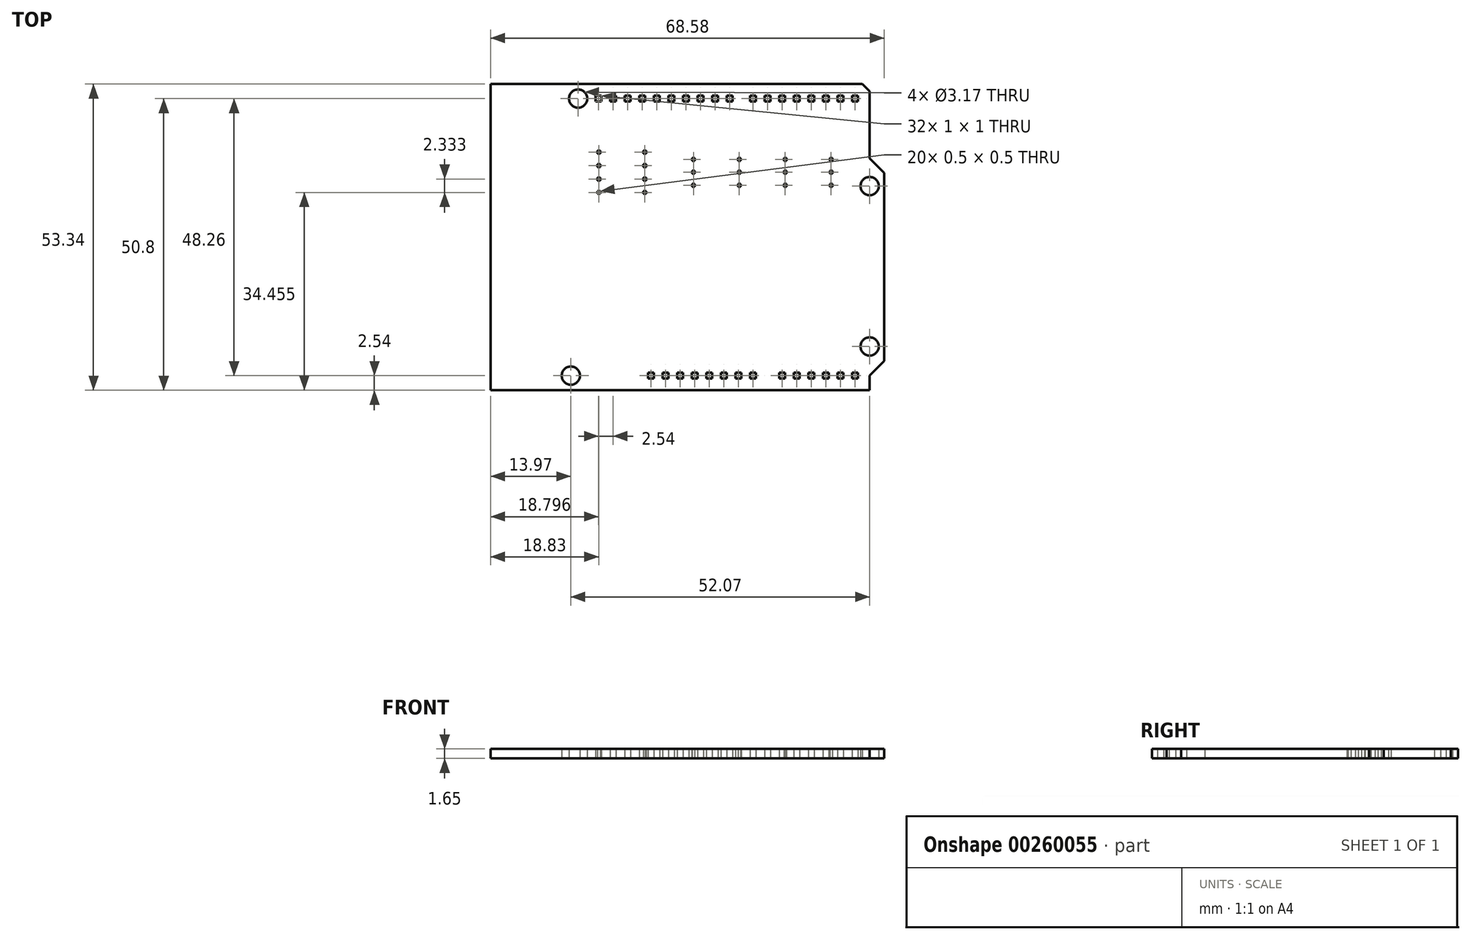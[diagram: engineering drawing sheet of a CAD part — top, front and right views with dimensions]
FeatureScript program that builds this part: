
annotation { "Feature Type Name" : "Feature", "Feature Type Description" : "" }
export const myFeature = defineFeature(function(context is Context, id is Id, definition is map)
    precondition{}
    {
        {
            var Q0;
            Q0=qCreatedBy(makeId("Top.planeOp"),FACE);
            var sketch = newSketch(context, id + "F0", { "sketchPlane" : qUnion([Q0])});
            skLineSegment(sketch, "E0", {"start": v(0, 0) * mm, "end": v(0, 53.34) * mm});
            skLineSegment(sketch, "E1", {"start": v(0, 53.34) * mm, "end": v(64.77, 53.34) * mm});
            skLineSegment(sketch, "E2", {"start": v(66.04, 52.07) * mm, "end": v(66.04, 40.39) * mm});
            skLineSegment(sketch, "E3", {"start": v(68.58, 37.85) * mm, "end": v(68.58, 5.08) * mm});
            skLineSegment(sketch, "E4", {"start": v(66.04, 0) * mm, "end": v(0, 0) * mm});
            skLineSegment(sketch, "E5", {"start": v(66.04, 40.39) * mm, "end": v(68.58, 37.85) * mm});
            skLineSegment(sketch, "E6", {"start": v(68.58, 5.08) * mm, "end": v(66.04, 2.54) * mm});
            skLineSegment(sketch, "E7", {"start": v(66.04, 2.54) * mm, "end": v(66.04, 0) * mm});
            skPoint(sketch, "E8.orphan", {"position": v(68.58, 0) * mm});
            skLineSegment(sketch, "E9", {"start": v(64.77, 53.34) * mm, "end": v(66.04, 52.07) * mm});
            skCircle(sketch, "E10", {"center": v(15.24, 50.8) * mm, "radius": 1.59 * mm});
            skCircle(sketch, "E11", {"center": v(66.04, 35.56) * mm, "radius": 1.59 * mm});
            skCircle(sketch, "E12", {"center": v(13.97, 2.54) * mm, "radius": 1.59 * mm});
            skCircle(sketch, "E13", {"center": v(66.04, 7.62) * mm, "radius": 1.59 * mm});
            skLineSegment(sketch, "E14.bottom", {"start": v(63, 3.04) * mm, "end": v(64, 3.04) * mm});
            skLineSegment(sketch, "E14.top", {"start": v(63, 2.04) * mm, "end": v(64, 2.04) * mm});
            skLineSegment(sketch, "E14.left", {"start": v(63, 3.04) * mm, "end": v(63, 2.04) * mm});
            skLineSegment(sketch, "E14.right", {"start": v(64, 3.04) * mm, "end": v(64, 2.04) * mm});
            skLineSegment(sketch, "E15", {"start": v(66.04, 2.54) * mm, "end": v(0, 2.54) * mm, "construction": true});
            skLineSegment(sketch, "E16.1.0.0", {"start": v(60.46, 3.04) * mm, "end": v(61.46, 3.04) * mm});
            skLineSegment(sketch, "E16.1.0.1", {"start": v(60.46, 3.04) * mm, "end": v(60.46, 2.04) * mm});
            skLineSegment(sketch, "E16.1.0.2", {"start": v(60.46, 2.04) * mm, "end": v(61.46, 2.04) * mm});
            skLineSegment(sketch, "E16.1.0.3", {"start": v(61.46, 3.04) * mm, "end": v(61.46, 2.04) * mm});
            skLineSegment(sketch, "E16.2.0.0", {"start": v(57.92, 3.04) * mm, "end": v(58.92, 3.04) * mm});
            skLineSegment(sketch, "E16.2.0.1", {"start": v(57.92, 3.04) * mm, "end": v(57.92, 2.04) * mm});
            skLineSegment(sketch, "E16.2.0.2", {"start": v(57.92, 2.04) * mm, "end": v(58.92, 2.04) * mm});
            skLineSegment(sketch, "E16.2.0.3", {"start": v(58.92, 3.04) * mm, "end": v(58.92, 2.04) * mm});
            skLineSegment(sketch, "E16.3.0.0", {"start": v(55.38, 3.04) * mm, "end": v(56.38, 3.04) * mm});
            skLineSegment(sketch, "E16.3.0.1", {"start": v(55.38, 3.04) * mm, "end": v(55.38, 2.04) * mm});
            skLineSegment(sketch, "E16.3.0.2", {"start": v(55.38, 2.04) * mm, "end": v(56.38, 2.04) * mm});
            skLineSegment(sketch, "E16.3.0.3", {"start": v(56.38, 3.04) * mm, "end": v(56.38, 2.04) * mm});
            skLineSegment(sketch, "E16.4.0.0", {"start": v(52.84, 3.04) * mm, "end": v(53.84, 3.04) * mm});
            skLineSegment(sketch, "E16.4.0.1", {"start": v(52.84, 3.04) * mm, "end": v(52.84, 2.04) * mm});
            skLineSegment(sketch, "E16.4.0.2", {"start": v(52.84, 2.04) * mm, "end": v(53.84, 2.04) * mm});
            skLineSegment(sketch, "E16.4.0.3", {"start": v(53.84, 3.04) * mm, "end": v(53.84, 2.04) * mm});
            skLineSegment(sketch, "E16.5.0.0", {"start": v(50.3, 3.04) * mm, "end": v(51.3, 3.04) * mm});
            skLineSegment(sketch, "E16.5.0.1", {"start": v(50.3, 3.04) * mm, "end": v(50.3, 2.04) * mm});
            skLineSegment(sketch, "E16.5.0.2", {"start": v(50.3, 2.04) * mm, "end": v(51.3, 2.04) * mm});
            skLineSegment(sketch, "E16.5.0.3", {"start": v(51.3, 3.04) * mm, "end": v(51.3, 2.04) * mm});
            skLineSegment(sketch, "E16.direction1", {"start": v(63, 3.04) * mm, "end": v(60.46, 3.04) * mm, "construction": true});
            skLineSegment(sketch, "E17.bottom", {"start": v(45.22, 3.04) * mm, "end": v(46.22, 3.04) * mm});
            skLineSegment(sketch, "E17.top", {"start": v(45.22, 2.04) * mm, "end": v(46.22, 2.04) * mm});
            skLineSegment(sketch, "E17.left", {"start": v(45.22, 3.04) * mm, "end": v(45.22, 2.04) * mm});
            skLineSegment(sketch, "E17.right", {"start": v(46.22, 3.04) * mm, "end": v(46.22, 2.04) * mm});
            skLineSegment(sketch, "E18.1.0.0", {"start": v(42.68, 3.04) * mm, "end": v(43.68, 3.04) * mm});
            skLineSegment(sketch, "E18.1.0.1", {"start": v(42.68, 3.04) * mm, "end": v(42.68, 2.04) * mm});
            skLineSegment(sketch, "E18.1.0.2", {"start": v(42.68, 2.04) * mm, "end": v(43.68, 2.04) * mm});
            skLineSegment(sketch, "E18.1.0.3", {"start": v(43.68, 3.04) * mm, "end": v(43.68, 2.04) * mm});
            skLineSegment(sketch, "E18.2.0.0", {"start": v(40.14, 3.04) * mm, "end": v(41.14, 3.04) * mm});
            skLineSegment(sketch, "E18.2.0.1", {"start": v(40.14, 3.04) * mm, "end": v(40.14, 2.04) * mm});
            skLineSegment(sketch, "E18.2.0.2", {"start": v(40.14, 2.04) * mm, "end": v(41.14, 2.04) * mm});
            skLineSegment(sketch, "E18.2.0.3", {"start": v(41.14, 3.04) * mm, "end": v(41.14, 2.04) * mm});
            skLineSegment(sketch, "E18.3.0.0", {"start": v(37.6, 3.04) * mm, "end": v(38.6, 3.04) * mm});
            skLineSegment(sketch, "E18.3.0.1", {"start": v(37.6, 3.04) * mm, "end": v(37.6, 2.04) * mm});
            skLineSegment(sketch, "E18.3.0.2", {"start": v(37.6, 2.04) * mm, "end": v(38.6, 2.04) * mm});
            skLineSegment(sketch, "E18.3.0.3", {"start": v(38.6, 3.04) * mm, "end": v(38.6, 2.04) * mm});
            skLineSegment(sketch, "E18.4.0.0", {"start": v(35.06, 3.04) * mm, "end": v(36.06, 3.04) * mm});
            skLineSegment(sketch, "E18.4.0.1", {"start": v(35.06, 3.04) * mm, "end": v(35.06, 2.04) * mm});
            skLineSegment(sketch, "E18.4.0.2", {"start": v(35.06, 2.04) * mm, "end": v(36.06, 2.04) * mm});
            skLineSegment(sketch, "E18.4.0.3", {"start": v(36.06, 3.04) * mm, "end": v(36.06, 2.04) * mm});
            skLineSegment(sketch, "E18.5.0.0", {"start": v(32.52, 3.04) * mm, "end": v(33.52, 3.04) * mm});
            skLineSegment(sketch, "E18.5.0.1", {"start": v(32.52, 3.04) * mm, "end": v(32.52, 2.04) * mm});
            skLineSegment(sketch, "E18.5.0.2", {"start": v(32.52, 2.04) * mm, "end": v(33.52, 2.04) * mm});
            skLineSegment(sketch, "E18.5.0.3", {"start": v(33.52, 3.04) * mm, "end": v(33.52, 2.04) * mm});
            skLineSegment(sketch, "E18.6.0.0", {"start": v(29.98, 3.04) * mm, "end": v(30.98, 3.04) * mm});
            skLineSegment(sketch, "E18.6.0.1", {"start": v(29.98, 3.04) * mm, "end": v(29.98, 2.04) * mm});
            skLineSegment(sketch, "E18.6.0.2", {"start": v(29.98, 2.04) * mm, "end": v(30.98, 2.04) * mm});
            skLineSegment(sketch, "E18.6.0.3", {"start": v(30.98, 3.04) * mm, "end": v(30.98, 2.04) * mm});
            skLineSegment(sketch, "E18.7.0.0", {"start": v(27.44, 3.04) * mm, "end": v(28.44, 3.04) * mm});
            skLineSegment(sketch, "E18.7.0.1", {"start": v(27.44, 3.04) * mm, "end": v(27.44, 2.04) * mm});
            skLineSegment(sketch, "E18.7.0.2", {"start": v(27.44, 2.04) * mm, "end": v(28.44, 2.04) * mm});
            skLineSegment(sketch, "E18.7.0.3", {"start": v(28.44, 3.04) * mm, "end": v(28.44, 2.04) * mm});
            skLineSegment(sketch, "E18.direction1", {"start": v(45.22, 3.04) * mm, "end": v(42.68, 3.04) * mm, "construction": true});
            skLineSegment(sketch, "E19", {"start": v(66.04, 50.8) * mm, "end": v(0, 50.8) * mm, "construction": true});
            skLineSegment(sketch, "E20.bottom", {"start": v(63, 51.3) * mm, "end": v(64, 51.3) * mm});
            skLineSegment(sketch, "E20.top", {"start": v(63, 50.3) * mm, "end": v(64, 50.3) * mm});
            skLineSegment(sketch, "E20.left", {"start": v(63, 51.3) * mm, "end": v(63, 50.3) * mm});
            skLineSegment(sketch, "E20.right", {"start": v(64, 51.3) * mm, "end": v(64, 50.3) * mm});
            skLineSegment(sketch, "E21.1.0.0", {"start": v(60.46, 51.3) * mm, "end": v(60.46, 50.3) * mm});
            skLineSegment(sketch, "E21.1.0.1", {"start": v(60.46, 51.3) * mm, "end": v(61.46, 51.3) * mm});
            skLineSegment(sketch, "E21.1.0.2", {"start": v(61.46, 51.3) * mm, "end": v(61.46, 50.3) * mm});
            skLineSegment(sketch, "E21.1.0.3", {"start": v(60.46, 50.3) * mm, "end": v(61.46, 50.3) * mm});
            skLineSegment(sketch, "E21.2.0.0", {"start": v(57.92, 51.3) * mm, "end": v(57.92, 50.3) * mm});
            skLineSegment(sketch, "E21.2.0.1", {"start": v(57.92, 51.3) * mm, "end": v(58.92, 51.3) * mm});
            skLineSegment(sketch, "E21.2.0.2", {"start": v(58.92, 51.3) * mm, "end": v(58.92, 50.3) * mm});
            skLineSegment(sketch, "E21.2.0.3", {"start": v(57.92, 50.3) * mm, "end": v(58.92, 50.3) * mm});
            skLineSegment(sketch, "E21.3.0.0", {"start": v(55.38, 51.3) * mm, "end": v(55.38, 50.3) * mm});
            skLineSegment(sketch, "E21.3.0.1", {"start": v(55.38, 51.3) * mm, "end": v(56.38, 51.3) * mm});
            skLineSegment(sketch, "E21.3.0.2", {"start": v(56.38, 51.3) * mm, "end": v(56.38, 50.3) * mm});
            skLineSegment(sketch, "E21.3.0.3", {"start": v(55.38, 50.3) * mm, "end": v(56.38, 50.3) * mm});
            skLineSegment(sketch, "E21.4.0.0", {"start": v(52.84, 51.3) * mm, "end": v(52.84, 50.3) * mm});
            skLineSegment(sketch, "E21.4.0.1", {"start": v(52.84, 51.3) * mm, "end": v(53.84, 51.3) * mm});
            skLineSegment(sketch, "E21.4.0.2", {"start": v(53.84, 51.3) * mm, "end": v(53.84, 50.3) * mm});
            skLineSegment(sketch, "E21.4.0.3", {"start": v(52.84, 50.3) * mm, "end": v(53.84, 50.3) * mm});
            skLineSegment(sketch, "E21.5.0.0", {"start": v(50.3, 51.3) * mm, "end": v(50.3, 50.3) * mm});
            skLineSegment(sketch, "E21.5.0.1", {"start": v(50.3, 51.3) * mm, "end": v(51.3, 51.3) * mm});
            skLineSegment(sketch, "E21.5.0.2", {"start": v(51.3, 51.3) * mm, "end": v(51.3, 50.3) * mm});
            skLineSegment(sketch, "E21.5.0.3", {"start": v(50.3, 50.3) * mm, "end": v(51.3, 50.3) * mm});
            skLineSegment(sketch, "E21.6.0.0", {"start": v(47.76, 51.3) * mm, "end": v(47.76, 50.3) * mm});
            skLineSegment(sketch, "E21.6.0.1", {"start": v(47.76, 51.3) * mm, "end": v(48.76, 51.3) * mm});
            skLineSegment(sketch, "E21.6.0.2", {"start": v(48.76, 51.3) * mm, "end": v(48.76, 50.3) * mm});
            skLineSegment(sketch, "E21.6.0.3", {"start": v(47.76, 50.3) * mm, "end": v(48.76, 50.3) * mm});
            skLineSegment(sketch, "E21.7.0.0", {"start": v(45.22, 51.3) * mm, "end": v(45.22, 50.3) * mm});
            skLineSegment(sketch, "E21.7.0.1", {"start": v(45.22, 51.3) * mm, "end": v(46.22, 51.3) * mm});
            skLineSegment(sketch, "E21.7.0.2", {"start": v(46.22, 51.3) * mm, "end": v(46.22, 50.3) * mm});
            skLineSegment(sketch, "E21.7.0.3", {"start": v(45.22, 50.3) * mm, "end": v(46.22, 50.3) * mm});
            skLineSegment(sketch, "E21.direction1", {"start": v(63, 50.3) * mm, "end": v(60.46, 50.3) * mm, "construction": true});
            skLineSegment(sketch, "E22.bottom", {"start": v(41.16, 51.3) * mm, "end": v(42.16, 51.3) * mm});
            skLineSegment(sketch, "E22.top", {"start": v(41.16, 50.3) * mm, "end": v(42.16, 50.3) * mm});
            skLineSegment(sketch, "E22.left", {"start": v(41.16, 51.3) * mm, "end": v(41.16, 50.3) * mm});
            skLineSegment(sketch, "E22.right", {"start": v(42.16, 51.3) * mm, "end": v(42.16, 50.3) * mm});
            skLineSegment(sketch, "E23.1.0.0", {"start": v(38.62, 51.3) * mm, "end": v(39.62, 51.3) * mm});
            skLineSegment(sketch, "E23.1.0.1", {"start": v(38.62, 51.3) * mm, "end": v(38.62, 50.3) * mm});
            skLineSegment(sketch, "E23.1.0.2", {"start": v(38.62, 50.3) * mm, "end": v(39.62, 50.3) * mm});
            skLineSegment(sketch, "E23.1.0.3", {"start": v(39.62, 51.3) * mm, "end": v(39.62, 50.3) * mm});
            skLineSegment(sketch, "E23.2.0.0", {"start": v(36.08, 51.3) * mm, "end": v(37.08, 51.3) * mm});
            skLineSegment(sketch, "E23.2.0.1", {"start": v(36.08, 51.3) * mm, "end": v(36.08, 50.3) * mm});
            skLineSegment(sketch, "E23.2.0.2", {"start": v(36.08, 50.3) * mm, "end": v(37.08, 50.3) * mm});
            skLineSegment(sketch, "E23.2.0.3", {"start": v(37.08, 51.3) * mm, "end": v(37.08, 50.3) * mm});
            skLineSegment(sketch, "E23.3.0.0", {"start": v(33.54, 51.3) * mm, "end": v(34.54, 51.3) * mm});
            skLineSegment(sketch, "E23.3.0.1", {"start": v(33.54, 51.3) * mm, "end": v(33.54, 50.3) * mm});
            skLineSegment(sketch, "E23.3.0.2", {"start": v(33.54, 50.3) * mm, "end": v(34.54, 50.3) * mm});
            skLineSegment(sketch, "E23.3.0.3", {"start": v(34.54, 51.3) * mm, "end": v(34.54, 50.3) * mm});
            skLineSegment(sketch, "E23.4.0.0", {"start": v(31, 51.3) * mm, "end": v(32, 51.3) * mm});
            skLineSegment(sketch, "E23.4.0.1", {"start": v(31, 51.3) * mm, "end": v(31, 50.3) * mm});
            skLineSegment(sketch, "E23.4.0.2", {"start": v(31, 50.3) * mm, "end": v(32, 50.3) * mm});
            skLineSegment(sketch, "E23.4.0.3", {"start": v(32, 51.3) * mm, "end": v(32, 50.3) * mm});
            skLineSegment(sketch, "E23.5.0.0", {"start": v(28.46, 51.3) * mm, "end": v(29.46, 51.3) * mm});
            skLineSegment(sketch, "E23.5.0.1", {"start": v(28.46, 51.3) * mm, "end": v(28.46, 50.3) * mm});
            skLineSegment(sketch, "E23.5.0.2", {"start": v(28.46, 50.3) * mm, "end": v(29.46, 50.3) * mm});
            skLineSegment(sketch, "E23.5.0.3", {"start": v(29.46, 51.3) * mm, "end": v(29.46, 50.3) * mm});
            skLineSegment(sketch, "E23.6.0.0", {"start": v(25.92, 51.3) * mm, "end": v(26.92, 51.3) * mm});
            skLineSegment(sketch, "E23.6.0.1", {"start": v(25.92, 51.3) * mm, "end": v(25.92, 50.3) * mm});
            skLineSegment(sketch, "E23.6.0.2", {"start": v(25.92, 50.3) * mm, "end": v(26.92, 50.3) * mm});
            skLineSegment(sketch, "E23.6.0.3", {"start": v(26.92, 51.3) * mm, "end": v(26.92, 50.3) * mm});
            skLineSegment(sketch, "E23.7.0.0", {"start": v(23.38, 51.3) * mm, "end": v(24.38, 51.3) * mm});
            skLineSegment(sketch, "E23.7.0.1", {"start": v(23.38, 51.3) * mm, "end": v(23.38, 50.3) * mm});
            skLineSegment(sketch, "E23.7.0.2", {"start": v(23.38, 50.3) * mm, "end": v(24.38, 50.3) * mm});
            skLineSegment(sketch, "E23.7.0.3", {"start": v(24.38, 51.3) * mm, "end": v(24.38, 50.3) * mm});
            skLineSegment(sketch, "E23.8.0.0", {"start": v(20.84, 51.3) * mm, "end": v(21.84, 51.3) * mm});
            skLineSegment(sketch, "E23.8.0.1", {"start": v(20.84, 51.3) * mm, "end": v(20.84, 50.3) * mm});
            skLineSegment(sketch, "E23.8.0.2", {"start": v(20.84, 50.3) * mm, "end": v(21.84, 50.3) * mm});
            skLineSegment(sketch, "E23.8.0.3", {"start": v(21.84, 51.3) * mm, "end": v(21.84, 50.3) * mm});
            skLineSegment(sketch, "E23.9.0.0", {"start": v(18.3, 51.3) * mm, "end": v(19.3, 51.3) * mm});
            skLineSegment(sketch, "E23.9.0.1", {"start": v(18.3, 51.3) * mm, "end": v(18.3, 50.3) * mm});
            skLineSegment(sketch, "E23.9.0.2", {"start": v(18.3, 50.3) * mm, "end": v(19.3, 50.3) * mm});
            skLineSegment(sketch, "E23.9.0.3", {"start": v(19.3, 51.3) * mm, "end": v(19.3, 50.3) * mm});
            skLineSegment(sketch, "E23.direction1", {"start": v(41.16, 51.3) * mm, "end": v(38.62, 51.3) * mm, "construction": true});
            skLineSegment(sketch, "E24.bottom", {"start": v(55.58, 41.7) * mm, "end": v(61.58, 41.7) * mm, "construction": true});
            skLineSegment(sketch, "E24.top", {"start": v(55.58, 34.2) * mm, "end": v(61.58, 34.2) * mm, "construction": true});
            skLineSegment(sketch, "E24.left", {"start": v(55.58, 41.7) * mm, "end": v(55.58, 34.2) * mm, "construction": true});
            skLineSegment(sketch, "E24.right", {"start": v(61.58, 41.7) * mm, "end": v(61.58, 34.2) * mm, "construction": true});
            skLineSegment(sketch, "E25.bottom", {"start": v(59.08, 40.46) * mm, "end": v(59.58, 40.46) * mm});
            skLineSegment(sketch, "E25.top", {"start": v(59.08, 35.46) * mm, "end": v(59.58, 35.46) * mm});
            skLineSegment(sketch, "E25.left", {"start": v(59.08, 40.46) * mm, "end": v(59.08, 39.96) * mm});
            skLineSegment(sketch, "E25.right", {"start": v(59.58, 40.46) * mm, "end": v(59.58, 39.96) * mm});
            skLineSegment(sketch, "E26", {"start": v(59.08, 39.96) * mm, "end": v(59.58, 39.96) * mm});
            skLineSegment(sketch, "E27", {"start": v(59.08, 38.2) * mm, "end": v(59.58, 38.2) * mm});
            skLineSegment(sketch, "E28", {"start": v(59.08, 37.7) * mm, "end": v(59.58, 37.7) * mm});
            skLineSegment(sketch, "E29", {"start": v(59.08, 35.96) * mm, "end": v(59.58, 35.96) * mm});
            skLineSegment(sketch, "E30.trimOffspring", {"start": v(59.08, 38.2) * mm, "end": v(59.08, 37.7) * mm});
            skLineSegment(sketch, "E31.trimOffspring", {"start": v(59.58, 38.2) * mm, "end": v(59.58, 37.7) * mm});
            skLineSegment(sketch, "E32.trimOffspring", {"start": v(59.08, 35.96) * mm, "end": v(59.08, 35.46) * mm});
            skLineSegment(sketch, "E33.trimOffspring", {"start": v(59.58, 35.96) * mm, "end": v(59.58, 35.46) * mm});
            skLineSegment(sketch, "E34", {"start": v(55.58, 37.96) * mm, "end": v(61.58, 37.96) * mm, "construction": true});
            skLineSegment(sketch, "E35.1.0.0", {"start": v(51.08, 40.46) * mm, "end": v(51.58, 40.46) * mm});
            skLineSegment(sketch, "E35.1.0.1", {"start": v(51.08, 40.46) * mm, "end": v(51.08, 39.96) * mm});
            skLineSegment(sketch, "E35.1.0.2", {"start": v(51.08, 39.96) * mm, "end": v(51.58, 39.96) * mm});
            skLineSegment(sketch, "E35.1.0.3", {"start": v(51.58, 40.46) * mm, "end": v(51.58, 39.96) * mm});
            skLineSegment(sketch, "E35.1.0.4", {"start": v(51.08, 38.2) * mm, "end": v(51.58, 38.2) * mm});
            skLineSegment(sketch, "E35.1.0.5", {"start": v(51.08, 38.2) * mm, "end": v(51.08, 37.7) * mm});
            skLineSegment(sketch, "E35.1.0.6", {"start": v(51.58, 38.2) * mm, "end": v(51.58, 37.7) * mm});
            skLineSegment(sketch, "E35.1.0.7", {"start": v(51.08, 37.7) * mm, "end": v(51.58, 37.7) * mm});
            skLineSegment(sketch, "E35.1.0.8", {"start": v(51.08, 35.96) * mm, "end": v(51.58, 35.96) * mm});
            skLineSegment(sketch, "E35.1.0.9", {"start": v(51.08, 35.96) * mm, "end": v(51.08, 35.46) * mm});
            skLineSegment(sketch, "E35.1.0.10", {"start": v(51.08, 35.46) * mm, "end": v(51.58, 35.46) * mm});
            skLineSegment(sketch, "E35.1.0.11", {"start": v(51.58, 35.96) * mm, "end": v(51.58, 35.46) * mm});
            skLineSegment(sketch, "E35.2.0.0", {"start": v(43.08, 40.46) * mm, "end": v(43.58, 40.46) * mm});
            skLineSegment(sketch, "E35.2.0.1", {"start": v(43.08, 40.46) * mm, "end": v(43.08, 39.96) * mm});
            skLineSegment(sketch, "E35.2.0.2", {"start": v(43.08, 39.96) * mm, "end": v(43.58, 39.96) * mm});
            skLineSegment(sketch, "E35.2.0.3", {"start": v(43.58, 40.46) * mm, "end": v(43.58, 39.96) * mm});
            skLineSegment(sketch, "E35.2.0.4", {"start": v(43.08, 38.2) * mm, "end": v(43.58, 38.2) * mm});
            skLineSegment(sketch, "E35.2.0.5", {"start": v(43.08, 38.2) * mm, "end": v(43.08, 37.7) * mm});
            skLineSegment(sketch, "E35.2.0.6", {"start": v(43.58, 38.2) * mm, "end": v(43.58, 37.7) * mm});
            skLineSegment(sketch, "E35.2.0.7", {"start": v(43.08, 37.7) * mm, "end": v(43.58, 37.7) * mm});
            skLineSegment(sketch, "E35.2.0.8", {"start": v(43.08, 35.96) * mm, "end": v(43.58, 35.96) * mm});
            skLineSegment(sketch, "E35.2.0.9", {"start": v(43.08, 35.96) * mm, "end": v(43.08, 35.46) * mm});
            skLineSegment(sketch, "E35.2.0.10", {"start": v(43.08, 35.46) * mm, "end": v(43.58, 35.46) * mm});
            skLineSegment(sketch, "E35.2.0.11", {"start": v(43.58, 35.96) * mm, "end": v(43.58, 35.46) * mm});
            skLineSegment(sketch, "E35.3.0.0", {"start": v(35.08, 40.46) * mm, "end": v(35.58, 40.46) * mm});
            skLineSegment(sketch, "E35.3.0.1", {"start": v(35.08, 40.46) * mm, "end": v(35.08, 39.96) * mm});
            skLineSegment(sketch, "E35.3.0.2", {"start": v(35.08, 39.96) * mm, "end": v(35.58, 39.96) * mm});
            skLineSegment(sketch, "E35.3.0.3", {"start": v(35.58, 40.46) * mm, "end": v(35.58, 39.96) * mm});
            skLineSegment(sketch, "E35.3.0.4", {"start": v(35.08, 38.2) * mm, "end": v(35.58, 38.2) * mm});
            skLineSegment(sketch, "E35.3.0.5", {"start": v(35.08, 38.2) * mm, "end": v(35.08, 37.7) * mm});
            skLineSegment(sketch, "E35.3.0.6", {"start": v(35.58, 38.2) * mm, "end": v(35.58, 37.7) * mm});
            skLineSegment(sketch, "E35.3.0.7", {"start": v(35.08, 37.7) * mm, "end": v(35.58, 37.7) * mm});
            skLineSegment(sketch, "E35.3.0.8", {"start": v(35.08, 35.96) * mm, "end": v(35.58, 35.96) * mm});
            skLineSegment(sketch, "E35.3.0.9", {"start": v(35.08, 35.96) * mm, "end": v(35.08, 35.46) * mm});
            skLineSegment(sketch, "E35.3.0.10", {"start": v(35.08, 35.46) * mm, "end": v(35.58, 35.46) * mm});
            skLineSegment(sketch, "E35.3.0.11", {"start": v(35.58, 35.96) * mm, "end": v(35.58, 35.46) * mm});
            skLineSegment(sketch, "E35.direction1", {"start": v(59.08, 40.46) * mm, "end": v(51.08, 40.46) * mm, "construction": true});
            skLineSegment(sketch, "E36.bottom", {"start": v(26.58, 41.7) * mm, "end": v(27.08, 41.7) * mm});
            skLineSegment(sketch, "E36.top", {"start": v(26.58, 34.2) * mm, "end": v(27.08, 34.2) * mm});
            skLineSegment(sketch, "E36.left", {"start": v(26.58, 41.7) * mm, "end": v(26.58, 41.2) * mm});
            skLineSegment(sketch, "E36.right", {"start": v(27.08, 41.7) * mm, "end": v(27.08, 41.2) * mm});
            skLineSegment(sketch, "E37", {"start": v(26.58, 41.2) * mm, "end": v(27.08, 41.2) * mm});
            skLineSegment(sketch, "E38", {"start": v(26.58, 34.7) * mm, "end": v(27.08, 34.7) * mm});
            skLineSegment(sketch, "E39", {"start": v(26.58, 39.37) * mm, "end": v(27.08, 39.37) * mm});
            skLineSegment(sketch, "E40", {"start": v(26.58, 38.87) * mm, "end": v(27.08, 38.87) * mm});
            skLineSegment(sketch, "E41", {"start": v(26.58, 37.04) * mm, "end": v(27.08, 37.04) * mm});
            skLineSegment(sketch, "E42", {"start": v(26.58, 36.54) * mm, "end": v(27.08, 36.54) * mm});
            skLineSegment(sketch, "E43.trimOffspring", {"start": v(26.58, 39.37) * mm, "end": v(26.58, 38.87) * mm});
            skLineSegment(sketch, "E44.trimOffspring", {"start": v(27.08, 39.37) * mm, "end": v(27.08, 38.87) * mm});
            skLineSegment(sketch, "E45.trimOffspring", {"start": v(26.58, 37.04) * mm, "end": v(26.58, 36.54) * mm});
            skLineSegment(sketch, "E46.trimOffspring", {"start": v(27.08, 37.04) * mm, "end": v(27.08, 36.54) * mm});
            skLineSegment(sketch, "E47.trimOffspring", {"start": v(26.58, 34.7) * mm, "end": v(26.58, 34.2) * mm});
            skLineSegment(sketch, "E48.trimOffspring", {"start": v(27.08, 34.7) * mm, "end": v(27.08, 34.2) * mm});
            skLineSegment(sketch, "E49", {"start": v(35.08, 37.96) * mm, "end": v(0, 37.96) * mm, "construction": true});
            skLineSegment(sketch, "E50.bottom", {"start": v(18.58, 41.7) * mm, "end": v(19.08, 41.7) * mm});
            skLineSegment(sketch, "E50.top", {"start": v(18.58, 34.2) * mm, "end": v(19.08, 34.2) * mm});
            skLineSegment(sketch, "E50.left", {"start": v(18.58, 41.7) * mm, "end": v(18.58, 41.2) * mm});
            skLineSegment(sketch, "E50.right", {"start": v(19.08, 41.7) * mm, "end": v(19.08, 41.2) * mm});
            skLineSegment(sketch, "E51", {"start": v(18.58, 41.2) * mm, "end": v(19.08, 41.2) * mm});
            skLineSegment(sketch, "E52", {"start": v(18.58, 39.37) * mm, "end": v(19.08, 39.37) * mm});
            skLineSegment(sketch, "E53", {"start": v(18.58, 38.87) * mm, "end": v(19.08, 38.87) * mm});
            skLineSegment(sketch, "E54", {"start": v(18.58, 37.04) * mm, "end": v(19.08, 37.04) * mm});
            skLineSegment(sketch, "E55", {"start": v(18.58, 36.54) * mm, "end": v(19.08, 36.54) * mm});
            skLineSegment(sketch, "E56", {"start": v(18.58, 34.7) * mm, "end": v(19.08, 34.7) * mm});
            skLineSegment(sketch, "E57.trimOffspring", {"start": v(18.58, 39.37) * mm, "end": v(18.58, 38.87) * mm});
            skLineSegment(sketch, "E58.trimOffspring", {"start": v(19.08, 39.37) * mm, "end": v(19.08, 38.87) * mm});
            skLineSegment(sketch, "E59.trimOffspring", {"start": v(18.58, 37.04) * mm, "end": v(18.58, 36.54) * mm});
            skLineSegment(sketch, "E60.trimOffspring", {"start": v(19.08, 37.04) * mm, "end": v(19.08, 36.54) * mm});
            skLineSegment(sketch, "E61.trimOffspring", {"start": v(18.58, 34.7) * mm, "end": v(18.58, 34.2) * mm});
            skLineSegment(sketch, "E62.trimOffspring", {"start": v(19.08, 34.7) * mm, "end": v(19.08, 34.2) * mm});
            skSolve(sketch);
        }
        {
            var Q0;
            Q0=makeQuery(id+"F0.imprint","IMPRINT",FACE,{"disambiguationData":[TD([[makeQuery(id+"F0.imprint","IMPRINT",EDGE,{"derivedFrom":sQuery(id+"F0.wireOp",EDGE,"E0")}),-1.0]])]});
            extrude(context, id + "F1", {"entities" : qUnion([Q0]), "depth" : 1.65 * mm});
        }
    });
